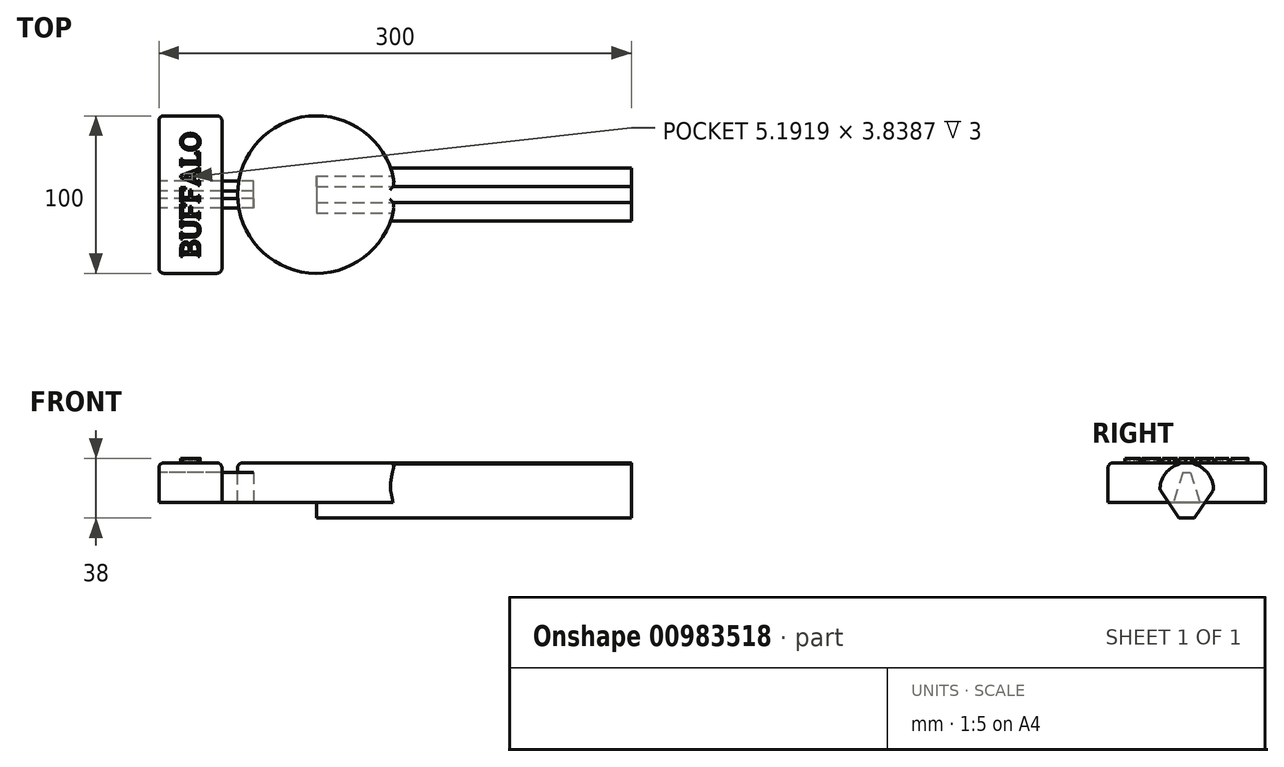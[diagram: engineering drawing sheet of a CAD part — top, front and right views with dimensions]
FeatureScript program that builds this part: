
annotation { "Feature Type Name" : "Feature", "Feature Type Description" : "" }
export const myFeature = defineFeature(function(context is Context, id is Id, definition is map)
    precondition{}
    {
        {
            var Q0;
            Q0=qCreatedBy(makeId("Top.planeOp"),FACE);
            var sketch = newSketch(context, id + "F0", { "sketchPlane" : qUnion([Q0])});
            skLineSegment(sketch, "E0.bottom", {"start": v(-72.75, -13.42) * mm, "end": v(127.25, -13.42) * mm});
            skLineSegment(sketch, "E0.top", {"start": v(-72.75, -23.42) * mm, "end": v(127.25, -23.42) * mm});
            skLineSegment(sketch, "E0.left", {"start": v(-72.75, -13.42) * mm, "end": v(-72.75, -23.42) * mm});
            skLineSegment(sketch, "E0.right", {"start": v(127.25, -13.42) * mm, "end": v(127.25, -23.42) * mm});
            skSolve(sketch);
        }
        {
            var Q0;
            Q0=makeQuery(id+"F0.imprint","IMPRINT",FACE,{"disambiguationData":[TD([[makeQuery(id+"F0.imprint","IMPRINT",EDGE,{"derivedFrom":sQuery(id+"F0.wireOp",EDGE,"E0.bottom")}),-1.0]])]});
            extrude(context, id + "F1", {"entities" : qUnion([Q0]), "depth" : 35 * mm, "offsetDistance" : 25 * mm});
        }
        {
            var Q0;
            Q0=makeQuery(id+"F1.opExtrude","SWEPT_FACE",FACE,{"disambiguationData":[OSD([sQuery(id+"F0.wireOp",EDGE,"E0.right")])]});
            var sketch = newSketch(context, id + "F2", { "sketchPlane" : qUnion([Q0])});
            skArc(sketch, "E1", {"start": v(-1.42, 18) * mm, "mid": v(-18.42, 35) * mm, "end": v(-35.42, 18) * mm});
            skPoint(sketch, "E2.start.orphan", {"position": v(-18.42, 35) * mm});
            skLineSegment(sketch, "E3", {"start": v(-18.42, 18) * mm, "end": v(-1.42, 18) * mm});
            skLineSegment(sketch, "E4", {"start": v(-1.42, 18) * mm, "end": v(-18.42, 18) * mm});
            skLineSegment(sketch, "E5", {"start": v(-35.42, 18) * mm, "end": v(-18.42, 18) * mm});
            skLineSegment(sketch, "E6", {"start": v(-23.42, 0) * mm, "end": v(-35.42, 18) * mm});
            skLineSegment(sketch, "E7", {"start": v(-13.42, 0) * mm, "end": v(-1.42, 18) * mm});
            skSolve(sketch);
        }
        {
            var Q0;
            {var subQ0=sQuery(id+"F2.wireOp",EDGE,"E5");var subQ1=sQuery(id+"F2.wireOp",EDGE,"E1");var subQ2=makeQuery(id+"F2.imprint","INTERSECT",VERTEX,{"derivedFrom":[subQ1,subQ0,sQuery(id+"F2.wireOp",EDGE,"E6")]});Q0=makeQuery(id+"F2.imprint","IMPRINT",FACE,{"disambiguationData":[TD([[makeQuery(id+"F2.imprint","IMPRINT",EDGE,{"disambiguationData":[TD([[subQ2,1.0]])],"derivedFrom":subQ1}),1.0]])]});}
            var Q1;
            {var subQ0=sQuery(id+"F2.wireOp",EDGE,"E4");var subQ1=sQuery(id+"F2.wireOp",EDGE,"E1");var subQ2=makeQuery(id+"F2.imprint","INTERSECT",VERTEX,{"derivedFrom":[subQ1,subQ0,sQuery(id+"F2.wireOp",EDGE,"E7")]});Q1=makeQuery(id+"F2.imprint","IMPRINT",FACE,{"disambiguationData":[TD([[makeQuery(id+"F2.imprint","IMPRINT",EDGE,{"disambiguationData":[TD([[subQ2,-1.0]])],"derivedFrom":subQ1}),1.0]])]});}
            var Q2;
            {var subQ0=sQuery(id+"F2.wireOp",EDGE,"E7");Q2=makeQuery(id+"F2.imprint","IMPRINT",FACE,{"disambiguationData":[TD([[makeQuery(id+"F2.imprint","IMPRINT",EDGE,{"derivedFrom":subQ0}),1.0]])]});}
            var Q3;
            {var subQ0=sQuery(id+"F2.wireOp",EDGE,"E6");Q3=makeQuery(id+"F2.imprint","IMPRINT",FACE,{"disambiguationData":[TD([[makeQuery(id+"F2.imprint","IMPRINT",EDGE,{"derivedFrom":subQ0}),-1.0]])]});}
            extrude(context, id + "F3", {"entities" : qUnion([Q0, Q1, Q2, Q3]), "operationType" : NewBodyOperationType.ADD, "oppositeDirection" : true, "depth" : 200 * mm, "offsetDistance" : 25 * mm});
        }
        {
            var Q0;
            Q0=makeQuery(id+"F1.opExtrude","CAP_FACE",FACE,{"disambiguationData":[OSD([sQuery(id+"F0.wireOp",EDGE,"E0.bottom"),sQuery(id+"F0.wireOp",EDGE,"E0.top"),sQuery(id+"F0.wireOp",EDGE,"E0.left"),sQuery(id+"F0.wireOp",EDGE,"E0.right")])],"isStart":false});
            var sketch = newSketch(context, id + "F4", { "sketchPlane" : qUnion([Q0])});
            skCircle(sketch, "E8", {"center": v(-72.75, -18.42) * mm, "radius": 50 * mm});
            skLineSegment(sketch, "E9", {"start": v(-72.75, -18.42) * mm, "end": v(-172.75, -18.42) * mm});
            skLineSegment(sketch, "E10.bottom", {"start": v(-172.75, -18.42) * mm, "end": v(-132.75, -18.42) * mm});
            skLineSegment(sketch, "E10.top", {"start": v(-172.75, 31.58) * mm, "end": v(-132.75, 31.58) * mm});
            skLineSegment(sketch, "E10.left", {"start": v(-172.75, -18.42) * mm, "end": v(-172.75, 31.58) * mm});
            skLineSegment(sketch, "E10.right", {"start": v(-132.75, -18.42) * mm, "end": v(-132.75, 31.58) * mm});
            skLineSegment(sketch, "E11.top", {"start": v(-172.75, -68.42) * mm, "end": v(-132.75, -68.42) * mm});
            skLineSegment(sketch, "E11.left", {"start": v(-172.75, -18.42) * mm, "end": v(-172.75, -68.42) * mm});
            skLineSegment(sketch, "E11.right", {"start": v(-132.75, -18.42) * mm, "end": v(-132.75, -68.42) * mm});
            skSolve(sketch);
        }
        {
            var Q0;
            {var subQ5=makeQuery(id+"F1.opExtrude","CAP_EDGE",EDGE,{"disambiguationData":[OSD([sQuery(id+"F0.wireOp",EDGE,"E0.left")])],"isStart":false});Q0=makeQuery(id+"F4.imprint","IMPRINT",FACE,{"disambiguationData":[TD([[makeQuery(id+"F4.imprint","IMPRINT",EDGE,{"derivedFrom":subQ5}),-1.0]])]});}
            extrude(context, id + "F5", {"entities" : qUnion([Q0]), "operationType" : NewBodyOperationType.ADD, "oppositeDirection" : true, "depth" : 25 * mm, "offsetDistance" : 25 * mm});
        }
        {
            var Q0;
            Q0 = qSketchRegion(id + "F4", true);
            extrude(context, id + "F6", {"entities" : qUnion([Q0]), "operationType" : NewBodyOperationType.ADD, "oppositeDirection" : true, "depth" : 25 * mm, "offsetDistance" : 25 * mm});
        }
        {
            var Q0;
            Q0=makeQuery(id+"F6.opExtrude","SWEPT_FACE",FACE,{"disambiguationData":[OSD([sQuery(id+"F4.wireOp",EDGE,"E10.left"),sQuery(id+"F4.wireOp",EDGE,"E11.left")])]});
            var sketch = newSketch(context, id + "F7", { "sketchPlane" : qUnion([Q0])});
            skLineSegment(sketch, "E12.top", {"start": v(18.42, 10) * mm, "end": v(15.92, 10) * mm});
            skLineSegment(sketch, "E12.right", {"start": v(16.17, 29.05) * mm, "end": v(15.92, 10) * mm});
            skLineSegment(sketch, "E13", {"start": v(20.92, 29.05) * mm, "end": v(16.17, 29.05) * mm});
            skPoint(sketch, "E14.orphan", {"position": v(18.42, 10) * mm});
            skPoint(sketch, "E15.start.orphan", {"position": v(-31.58, 22.5) * mm});
            skPoint(sketch, "E16.trimOffspring.end.orphan", {"position": v(68.42, 22.5) * mm});
            skPoint(sketch, "E17.left.start.orphan", {"position": v(18.42, 35) * mm});
            skLineSegment(sketch, "E18", {"start": v(20.92, 29.05) * mm, "end": v(20.92, 10) * mm});
            skLineSegment(sketch, "E19", {"start": v(20.92, 10) * mm, "end": v(15.92, 10) * mm});
            skLineSegment(sketch, "E20", {"start": v(16.17, 29.05) * mm, "end": v(9.92, 10) * mm});
            skLineSegment(sketch, "E21", {"start": v(20.92, 29.05) * mm, "end": v(26.92, 10) * mm});
            skSolve(sketch);
        }
        {
            var Q0;
            {var subQ0=sQuery(id+"F7.wireOp",EDGE,"E12.right");Q0=makeQuery(id+"F7.imprint","IMPRINT",FACE,{"disambiguationData":[TD([[makeQuery(id+"F7.imprint","IMPRINT",EDGE,{"derivedFrom":subQ0}),-1.0]])]});}
            var Q1;
            {var subQ0=sQuery(id+"F7.wireOp",EDGE,"E12.right");Q1=makeQuery(id+"F7.imprint","IMPRINT",FACE,{"disambiguationData":[TD([[makeQuery(id+"F7.imprint","IMPRINT",EDGE,{"derivedFrom":subQ0}),1.0]])]});}
            var Q2;
            {var subQ0=sQuery(id+"F7.wireOp",EDGE,"E18");Q2=makeQuery(id+"F7.imprint","IMPRINT",FACE,{"disambiguationData":[TD([[makeQuery(id+"F7.imprint","IMPRINT",EDGE,{"derivedFrom":subQ0}),1.0]])]});}
            extrude(context, id + "F8", {"entities" : qUnion([Q0, Q1, Q2]), "oppositeDirection" : true, "depth" : 60 * mm, "offsetDistance" : 25 * mm});
        }
        {
            var Q0;
            Q0=makeQuery(id+"F5.opExtrude","CAP_EDGE",EDGE,{"disambiguationData":[OSD([sQuery(id+"F4.wireOp",EDGE,"E8")])],"isStart":true});
            var Q1;
            Q1=makeQuery(id+"F6.opExtrude","CAP_EDGE",EDGE,{"disambiguationData":[OSD([sQuery(id+"F4.wireOp",EDGE,"E10.left"),sQuery(id+"F4.wireOp",EDGE,"E11.left")])],"isStart":true});
            var Q2;
            Q2=makeQuery(id+"F6.opExtrude","CAP_EDGE",EDGE,{"disambiguationData":[OSD([sQuery(id+"F4.wireOp",EDGE,"E10.top")])],"isStart":true});
            var Q3;
            Q3=makeQuery(id+"F6.opExtrude","CAP_EDGE",EDGE,{"disambiguationData":[OSD([sQuery(id+"F4.wireOp",EDGE,"E10.right"),sQuery(id+"F4.wireOp",EDGE,"E11.right")])],"isStart":true});
            var Q4;
            Q4=makeQuery(id+"F6.opExtrude","CAP_EDGE",EDGE,{"disambiguationData":[OSD([sQuery(id+"F4.wireOp",EDGE,"E11.top")])],"isStart":true});
            var Q5;
            Q5=makeQuery(id+"F6.opExtrude","SWEPT_EDGE",EDGE,{"disambiguationData":[OSD([sQuery(id+"F4.wireOp",EDGE,"E11.top"),sQuery(id+"F4.wireOp",EDGE,"E11.left")])]});
            var Q6;
            Q6=makeQuery(id+"F6.opExtrude","SWEPT_EDGE",EDGE,{"disambiguationData":[OSD([sQuery(id+"F4.wireOp",EDGE,"E11.top"),sQuery(id+"F4.wireOp",EDGE,"E11.right")])]});
            var Q7;
            Q7=makeQuery(id+"F6.opExtrude","SWEPT_EDGE",EDGE,{"disambiguationData":[OSD([sQuery(id+"F4.wireOp",EDGE,"E10.top"),sQuery(id+"F4.wireOp",EDGE,"E10.left")])]});
            var Q8;
            Q8=makeQuery(id+"F6.opExtrude","SWEPT_EDGE",EDGE,{"disambiguationData":[OSD([sQuery(id+"F4.wireOp",EDGE,"E10.top"),sQuery(id+"F4.wireOp",EDGE,"E10.right")])]});
            var Q9;
            Q9=makeQuery(id+"F3.opExtrude","SWEPT_EDGE",EDGE,{"disambiguationData":[OSD([sQuery(id+"F2.wireOp",EDGE,"E1"),sQuery(id+"F2.wireOp",EDGE,"E4"),sQuery(id+"F2.wireOp",EDGE,"E7")])]});
            var Q10;
            Q10=makeQuery(id+"F1.opExtrude","CAP_EDGE",EDGE,{"disambiguationData":[OSD([sQuery(id+"F0.wireOp",EDGE,"E0.bottom")])],"isStart":false});
            var Q11;
            Q11=makeQuery(id+"F1.opExtrude","CAP_EDGE",EDGE,{"disambiguationData":[OSD([sQuery(id+"F0.wireOp",EDGE,"E0.top")])],"isStart":false});
            var Q12;
            Q12=makeQuery(id+"F3.opExtrude","SWEPT_EDGE",EDGE,{"disambiguationData":[OSD([sQuery(id+"F2.wireOp",EDGE,"E1"),sQuery(id+"F2.wireOp",EDGE,"E5"),sQuery(id+"F2.wireOp",EDGE,"E6")])]});
            fillet(context, id + "F9", {"entities" : qUnion([Q0, Q1, Q2, Q3, Q4, Q5, Q6, Q7, Q8, Q9, Q10, Q11, Q12]), "radius" : 3 * mm, "tangentPropagation" : true, "allowEdgeOverflow" : false});
        }
        {
            var Q0;
            Q0=makeQuery(id+"F6.opExtrude","CAP_FACE",FACE,{"disambiguationData":[OSD([sQuery(id+"F4.wireOp",EDGE,"E10.top"),sQuery(id+"F4.wireOp",EDGE,"E10.left"),sQuery(id+"F4.wireOp",EDGE,"E10.right"),sQuery(id+"F4.wireOp",EDGE,"E11.top"),sQuery(id+"F4.wireOp",EDGE,"E11.left"),sQuery(id+"F4.wireOp",EDGE,"E11.right")])],"isStart":true});
            var sketch = newSketch(context, id + "F10", { "sketchPlane" : qUnion([Q0])});
            skText(sketch, "E22", { "text": "BUFFALO", "fontName": "RobotoSlab-Regular.ttf"});
            const initialGuessF10  = {"E22": [-0.14675, -0.05842, 0, 1, 0.01225]};
            skSetInitialGuess(sketch, initialGuessF10);
            skSolve(sketch);
        }
        {
            var Q0;
            Q0 = qSketchRegion(id + "F10", true);
            var Q1;
            Q1=makeQuery(id+"F10.imprint","IMPRINT",FACE,{"disambiguationData":[TD([[makeQuery(id+"F10.imprint","IMPRINT",EDGE,{"derivedFrom":sQuery(id+"F10.wireOp",EDGE,"E22.sketch_text.stroke-0")}),1.0]])]});
            extrude(context, id + "F11", {"entities" : qUnion([Q0, Q1]), "operationType" : NewBodyOperationType.REMOVE, "oppositeDirection" : true, "depth" : 3 * mm, "offsetDistance" : 25 * mm});
        }
        {
            var Q0;
            Q0=makeQuery(id+"F11.boolean.opBoolean","SPLIT",FACE,{"disambiguationData":[TD([makeQuery(id+"F11.opExtrude","SWEPT_FACE",FACE,{"disambiguationData":[OSD([sQuery(id+"F10.wireOp",EDGE,"E22.sketch_text.stroke-23")])]})])],"derivedFrom":makeQuery(id+"F6.opExtrude","CAP_FACE",FACE,{"disambiguationData":[OSD([sQuery(id+"F4.wireOp",EDGE,"E10.top"),sQuery(id+"F4.wireOp",EDGE,"E10.left"),sQuery(id+"F4.wireOp",EDGE,"E10.right"),sQuery(id+"F4.wireOp",EDGE,"E11.top"),sQuery(id+"F4.wireOp",EDGE,"E11.left"),sQuery(id+"F4.wireOp",EDGE,"E11.right")])],"isStart":true})});
            var Q1;
            Q1=makeQuery(id+"F11.boolean.opBoolean","SPLIT",FACE,{"disambiguationData":[TD([makeQuery(id+"F11.opExtrude","SWEPT_FACE",FACE,{"disambiguationData":[OSD([sQuery(id+"F10.wireOp",EDGE,"E22.sketch_text.stroke-16")])]})])],"derivedFrom":makeQuery(id+"F6.opExtrude","CAP_FACE",FACE,{"disambiguationData":[OSD([sQuery(id+"F4.wireOp",EDGE,"E10.top"),sQuery(id+"F4.wireOp",EDGE,"E10.left"),sQuery(id+"F4.wireOp",EDGE,"E10.right"),sQuery(id+"F4.wireOp",EDGE,"E11.top"),sQuery(id+"F4.wireOp",EDGE,"E11.left"),sQuery(id+"F4.wireOp",EDGE,"E11.right")])],"isStart":true})});
            var Q2;
            Q2=makeQuery(id+"F11.boolean.opBoolean","SPLIT",FACE,{"disambiguationData":[TD([makeQuery(id+"F11.opExtrude","SWEPT_FACE",FACE,{"disambiguationData":[OSD([sQuery(id+"F10.wireOp",EDGE,"E22.sketch_text.stroke-106")])]})])],"derivedFrom":makeQuery(id+"F6.opExtrude","CAP_FACE",FACE,{"disambiguationData":[OSD([sQuery(id+"F4.wireOp",EDGE,"E10.top"),sQuery(id+"F4.wireOp",EDGE,"E10.left"),sQuery(id+"F4.wireOp",EDGE,"E10.right"),sQuery(id+"F4.wireOp",EDGE,"E11.top"),sQuery(id+"F4.wireOp",EDGE,"E11.left"),sQuery(id+"F4.wireOp",EDGE,"E11.right")])],"isStart":true})});
            var Q3;
            Q3=makeQuery(id+"F11.boolean.opBoolean","SPLIT",FACE,{"disambiguationData":[TD([makeQuery(id+"F11.opExtrude","SWEPT_FACE",FACE,{"disambiguationData":[OSD([sQuery(id+"F10.wireOp",EDGE,"E22.sketch_text.stroke-136")])]})])],"derivedFrom":makeQuery(id+"F6.opExtrude","CAP_FACE",FACE,{"disambiguationData":[OSD([sQuery(id+"F4.wireOp",EDGE,"E10.top"),sQuery(id+"F4.wireOp",EDGE,"E10.left"),sQuery(id+"F4.wireOp",EDGE,"E10.right"),sQuery(id+"F4.wireOp",EDGE,"E11.top"),sQuery(id+"F4.wireOp",EDGE,"E11.left"),sQuery(id+"F4.wireOp",EDGE,"E11.right")])],"isStart":true})});
            extrude(context, id + "F12", {"entities" : qUnion([Q0, Q1, Q2, Q3]), "operationType" : NewBodyOperationType.REMOVE, "oppositeDirection" : true, "depth" : 3 * mm, "offsetDistance" : 25 * mm});
        }
        {
            var Q0;
            Q0 = qSketchRegion(id + "F10", true);
            var Q1;
            {var subQ0=sQuery(id+"F10.wireOp",EDGE,"E22.sketch_text.stroke-139");var subQ1=sQuery(id+"F10.wireOp",EDGE,"E22.sketch_text.stroke-138");var subQ2=sQuery(id+"F10.wireOp",EDGE,"E22.sketch_text.stroke-137");var subQ3=sQuery(id+"F10.wireOp",EDGE,"E22.sketch_text.stroke-136");var subQ4=sQuery(id+"F10.wireOp",EDGE,"E22.sketch_text.stroke-140");var subQ5=sQuery(id+"F10.wireOp",EDGE,"E22.sketch_text.stroke-141");var subQ6=sQuery(id+"F10.wireOp",EDGE,"E22.sketch_text.stroke-142");var subQ7=sQuery(id+"F10.wireOp",EDGE,"E22.sketch_text.stroke-143");var subQ8=sQuery(id+"F10.wireOp",EDGE,"E22.sketch_text.stroke-144");var subQ9=sQuery(id+"F10.wireOp",EDGE,"E22.sketch_text.stroke-145");var subQ10=sQuery(id+"F4.wireOp",EDGE,"E11.right");var subQ11=sQuery(id+"F4.wireOp",EDGE,"E11.left");var subQ12=sQuery(id+"F4.wireOp",EDGE,"E11.top");var subQ13=sQuery(id+"F4.wireOp",EDGE,"E10.right");var subQ14=sQuery(id+"F4.wireOp",EDGE,"E10.left");var subQ15=sQuery(id+"F4.wireOp",EDGE,"E10.top");var subQ16=makeQuery(id+"F6.opExtrude","CAP_FACE",FACE,{"disambiguationData":[OSD([subQ15,subQ14,subQ13,subQ12,subQ11,subQ10])],"isStart":true});var subQ17=sQuery(id+"F10.wireOp",EDGE,"E22.sketch_text.stroke-106");var subQ18=sQuery(id+"F10.wireOp",EDGE,"E22.sketch_text.stroke-107");var subQ19=sQuery(id+"F10.wireOp",EDGE,"E22.sketch_text.stroke-108");var subQ20=sQuery(id+"F10.wireOp",EDGE,"E22.sketch_text.stroke-109");var subQ21=sQuery(id+"F10.wireOp",EDGE,"E22.sketch_text.stroke-26");var subQ22=sQuery(id+"F10.wireOp",EDGE,"E22.sketch_text.stroke-25");var subQ23=sQuery(id+"F10.wireOp",EDGE,"E22.sketch_text.stroke-24");var subQ24=sQuery(id+"F10.wireOp",EDGE,"E22.sketch_text.stroke-23");var subQ25=sQuery(id+"F10.wireOp",EDGE,"E22.sketch_text.stroke-27");var subQ26=sQuery(id+"F10.wireOp",EDGE,"E22.sketch_text.stroke-28");var subQ27=sQuery(id+"F10.wireOp",EDGE,"E22.sketch_text.stroke-29");var subQ28=sQuery(id+"F10.wireOp",EDGE,"E22.sketch_text.stroke-18");var subQ29=sQuery(id+"F10.wireOp",EDGE,"E22.sketch_text.stroke-17");var subQ30=sQuery(id+"F10.wireOp",EDGE,"E22.sketch_text.stroke-19");var subQ31=sQuery(id+"F10.wireOp",EDGE,"E22.sketch_text.stroke-16");var subQ32=sQuery(id+"F10.wireOp",EDGE,"E22.sketch_text.stroke-20");var subQ33=sQuery(id+"F10.wireOp",EDGE,"E22.sketch_text.stroke-21");var subQ34=sQuery(id+"F10.wireOp",EDGE,"E22.sketch_text.stroke-22");Q1=makeQuery(id+"F12.boolean.opBoolean","MERGE",FACE,{"derivedFrom":[makeQuery(id+"F11.boolean.opBoolean","COPY",FACE,{"derivedFrom":makeQuery(id+"F11.opExtrude","CAP_FACE",FACE,{"disambiguationData":[OSD([subQ15,subQ14,subQ13,subQ12,subQ11,subQ10,subQ31,subQ29,subQ28,subQ30,subQ32,subQ33,subQ34,subQ24,subQ23,subQ22,subQ21,subQ25,subQ26,subQ27,subQ17,subQ18,subQ19,subQ20,subQ3,subQ2,subQ1,subQ0,subQ4,subQ5,subQ6,subQ7,subQ8,subQ9])],"isStart":false})})],"fromTools":[makeQuery(id+"F12.opExtrude","CAP_FACE",FACE,{"disambiguationData":[OSD([subQ15,subQ14,subQ13,subQ12,subQ11,subQ10]),TDD([makeQuery(id+"F11.boolean.opBoolean","SPLIT",FACE,{"disambiguationData":[TD([makeQuery(id+"F11.opExtrude","SWEPT_FACE",FACE,{"disambiguationData":[OSD([subQ31])]})])],"derivedFrom":subQ16})])],"isStart":false}),makeQuery(id+"F12.opExtrude","CAP_FACE",FACE,{"disambiguationData":[OSD([subQ15,subQ14,subQ13,subQ12,subQ11,subQ10]),TDD([makeQuery(id+"F11.boolean.opBoolean","SPLIT",FACE,{"disambiguationData":[TD([makeQuery(id+"F11.opExtrude","SWEPT_FACE",FACE,{"disambiguationData":[OSD([subQ24])]})])],"derivedFrom":subQ16})])],"isStart":false}),makeQuery(id+"F12.opExtrude","CAP_FACE",FACE,{"disambiguationData":[OSD([subQ15,subQ14,subQ13,subQ12,subQ11,subQ10]),TDD([makeQuery(id+"F11.boolean.opBoolean","SPLIT",FACE,{"disambiguationData":[TD([makeQuery(id+"F11.opExtrude","SWEPT_FACE",FACE,{"disambiguationData":[OSD([subQ17])]})])],"derivedFrom":subQ16})])],"isStart":false}),makeQuery(id+"F12.opExtrude","CAP_FACE",FACE,{"disambiguationData":[OSD([subQ15,subQ14,subQ13,subQ12,subQ11,subQ10]),TDD([makeQuery(id+"F11.boolean.opBoolean","SPLIT",FACE,{"disambiguationData":[TD([makeQuery(id+"F11.opExtrude","SWEPT_FACE",FACE,{"disambiguationData":[OSD([subQ3])]})])],"derivedFrom":subQ16})])],"isStart":false})]});}
            extrude(context, id + "F13", {"entities" : qUnion([Q0, Q1]), "operationType" : NewBodyOperationType.ADD, "depth" : 3 * mm, "offsetDistance" : 25 * mm});
        }
    });
